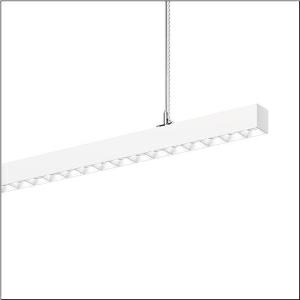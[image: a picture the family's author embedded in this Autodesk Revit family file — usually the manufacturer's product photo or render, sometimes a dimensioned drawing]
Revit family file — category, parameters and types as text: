
# Revit family: silica_r__21_51mx35da47wb_183f
name_source: partatom
category: Lighting Fixtures
units: mm (PartAtom-declared; Revit-internal decimal feet)

## family parameters
Cut with Voids When Loaded = No
Host = Face
Light Source = No
Part Type = Normal
Room Calculation Point = No
Round Connector Dimension = Use Diameter
Shared = No

## types (1)
- --- (1 x LED, 7080 lm, 40.6 W, 4000K)
    Apparent Load = 41 VA
    CIE Flux Codes = 84 98 100 61 100
    Color Rendering = 80
    Color Temperature = 4000K
    Default Elevation = 1800 mm
    Description = Silica® 21, office luminaire, primary light control with darklight reflector, of PMMA, white, CAT 2 (L<= 3000cd/m²), light emission: direct/indirect distribution, primary light characteristic: symmetric, installation type: suspended mounting, LED, rated luminous flux: 7.080lm, luminous efficacy: 174lm/W, light colour: 840, colour temperature: 4000K, with terminal, 3+2-pole, max. 2.5mm², mains connection: 220..240V, AC, 50/60Hz, rated input power: 40.6W, luminaire housing, of aluminium, traffic white (RAL 9016), length: 1.204mm, width: 53mm, height: 53mm, protection rating (complete): IP20, insulation class (complete): insulation class I (protective earthing), certification: CE, permissible operating ambient temperature: 0..+35°C, standard: EN 50419, packaging unit: 1 piece
    Height = 53 mm
    Lamp = 1 x LED
    Lamp Light Flux = 7080 lm
    Lamp Power = 40.6 W
    Lamp count = 1
    Length = 1204 mm
    Luminous efficacy = 174 lm/W
    Manufacturer = Siteco
    ModVariant = No
    Model = 51MX35DA47WB
    Mounting Place = Ceiling
    Mounting Type = Pendant
    Number of Poles = 1
    OnlyDefault = Yes
    Power Factor = 1
    Product Name = Silica® 21
    Product group = office luminaire | ceiling pendant
    ProductGroupID = 902
    Protection Class = Protection class I
    Protection Degree = IP 20
    RLX_Detail_Level = 1
    RLX_Emergency_Light_Flux = 0 lm
    RLX_Emergency_Type = 0
    RLX_Emergency_Type_DB = No
    RlxData = <blob elided: 40873 chars, md5=6c1f3098>
    Socket = socket
    Standby Power = 0 W
    System Light Flux = 7080 lm
    System Power = 41 W
    Type Comments = factory setting: luminous flux: 100 % | dim-lin: 254 | 339 mA
    Type Image = l_1297797.jpg
    URL = http://relux.com
    VarID = @adj_051209
    Voltage = 0 V
    Weight = 0.00 kg
    Width = 53 mm

## geometry (parser evidence)
native form markers: Blend x4, Sweep x12
no freeform markers — native parametric forms only
